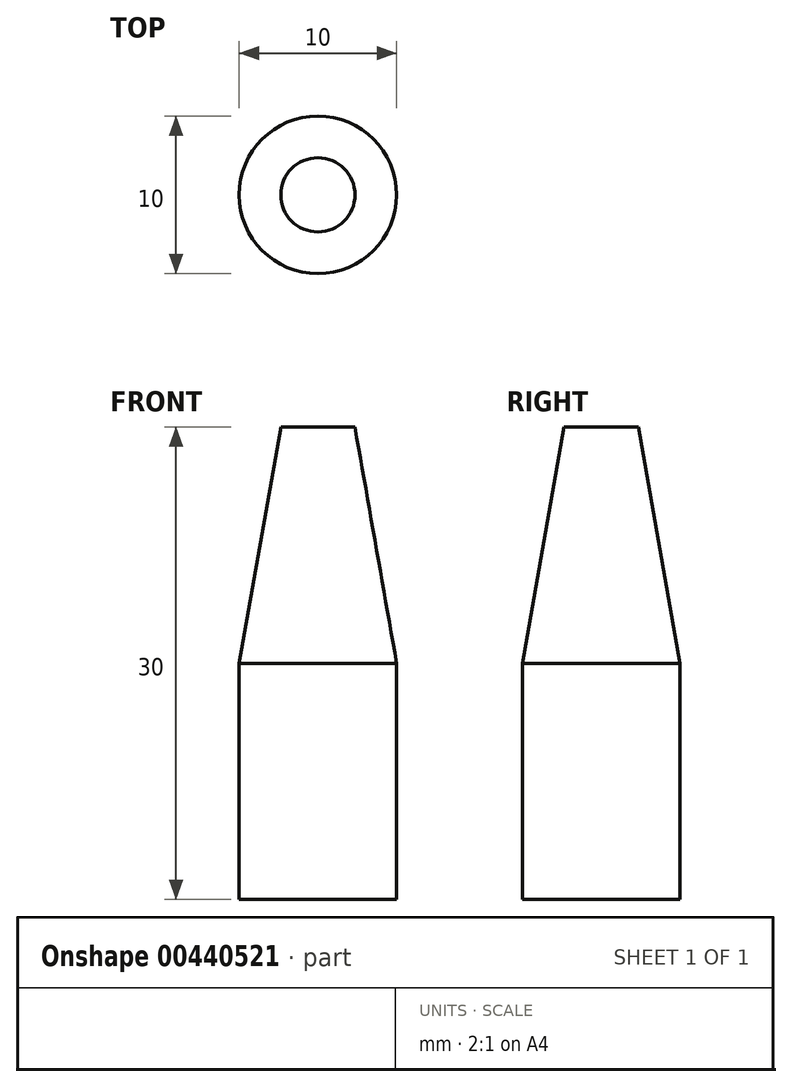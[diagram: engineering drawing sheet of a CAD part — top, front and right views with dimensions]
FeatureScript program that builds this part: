
annotation { "Feature Type Name" : "Feature", "Feature Type Description" : "" }
export const myFeature = defineFeature(function(context is Context, id is Id, definition is map)
    precondition{}
    {
        {
            var Q0;
            Q0=qCreatedBy(makeId("Top.planeOp"),FACE);
            var sketch = newSketch(context, id + "F0", { "sketchPlane" : qUnion([Q0])});
            skCircle(sketch, "E0", {"center": v(0, 0) * mm, "radius": 5 * mm});
            skSolve(sketch);
        }
        {
            var Q0;
            Q0=qSketchRegion(id+"F0",true);
            extrude(context, id + "F1", {"entities" : qUnion([Q0]), "depth" : 30 * mm});
        }
        {
            var Q0;
            Q0=makeQuery(id+"F1.opExtrude","CAP_EDGE",EDGE,{"disambiguationData":[OSD([sQuery(id+"F0.wireOp",EDGE,"E0")])],"isStart":false});
            chamfer(context, id + "F2", {"entities" : qUnion([Q0]), "chamferType" : ChamferType.OFFSET_ANGLE, "width" : 15 * mm, "oppositeDirection" : true, "angle" : 10 * degree, "tangentPropagation" : true});
        }
    });
